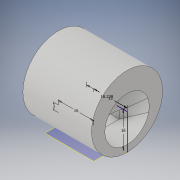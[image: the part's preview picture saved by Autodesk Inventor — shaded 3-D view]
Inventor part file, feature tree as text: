
AUTODESK INVENTOR PART (.ipt)
format: ipt  version: 2019 (Build 230136000, 136)  size: 233,984 bytes
history: native  units: in
note: dims shown in document units (in); Inventor stores cm internally (conversion verified against a paired STEP export)
features: sketch x7, extrude x2, revolve x1, loft x1, fillet x1, plane x1, other x1
ambient origin geometry x8: Origin, YZ Plane, XZ Plane, XY Plane, X Axis, Y Axis, Z Axis, Center Point
bodies: Solid1 (feature_tree)
feature tree (14):
  revolve  "Revolution1"  [1 undecoded]
  sketch  "Sketch2"  dims[d3=0.5906in d4=90.0deg]
  extrude  "Extrusion1"  TaperAngle=90.0deg  [1 undecoded]
  sketch  "Sketch4"  dims[d9=0.7874in d10=0.0in d11=90.0deg]
  sketch  "Sketch5"  dims[d12=0.0in d13=90.0deg]
  loft  "Loft1"
  fillet  "Fillet1"  Radius=0.1969in
  sketch  "Sketch6"  dims[d14=0.2362in]
  plane  "Work Plane1"
  extrude  "Extrusion2"  TaperAngle=0.0deg  [1 undecoded]
  sketch  "Sketch1"  dims[d0=0.1181in d1=0.6299in]
  sketch  "Sketch3"  dims[d5=0.1181in d6=0.5118in d7=0.1969in d8=0.0in]
  other  "Edges1"
  sketch  "Sketch7"  dims[d15=0.5118in d16=0.1969in d17=0.0in d18=0.6299in d19=0.7177in]
note: 3 required parameter values undecoded (feature->parameter linkage not recoverable at this tier; creation-order binding heuristic only, values carry confidence <= 0.55)